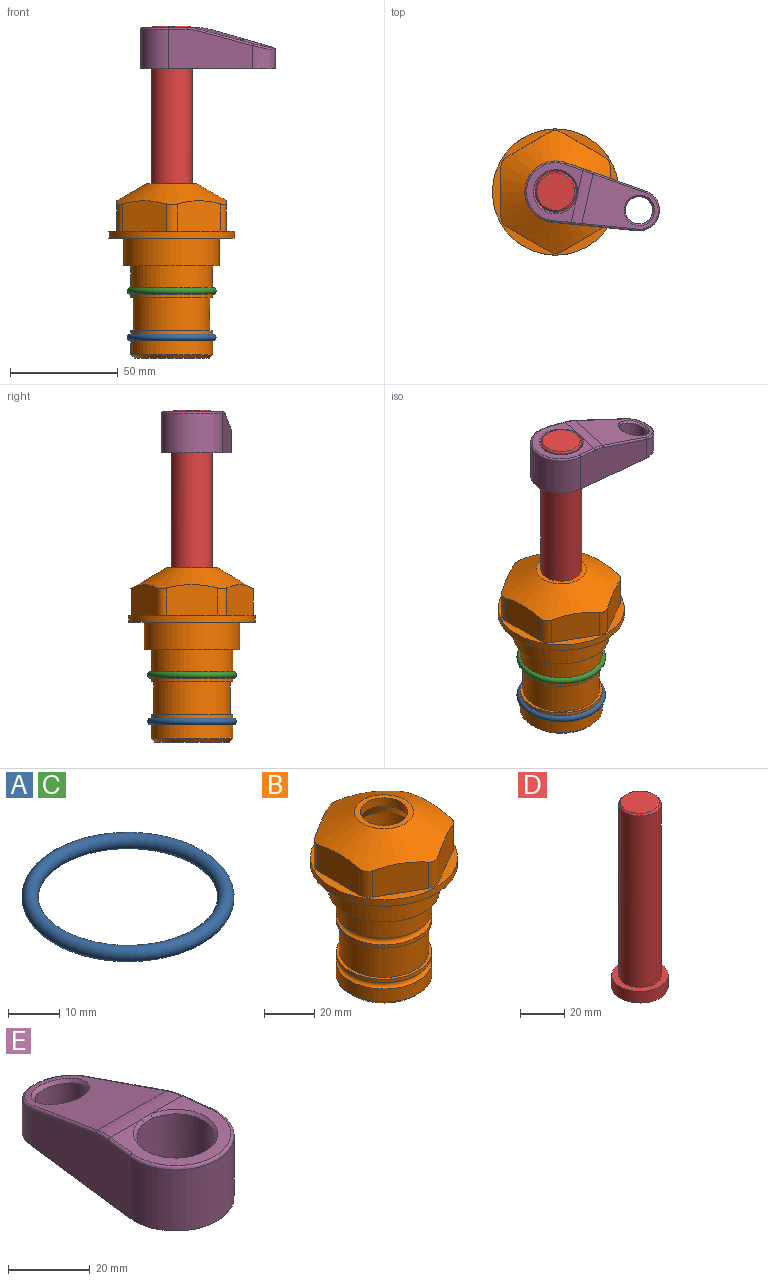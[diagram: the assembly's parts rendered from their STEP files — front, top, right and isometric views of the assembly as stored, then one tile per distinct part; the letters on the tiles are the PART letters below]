
ASSEMBLY  parts=5 mates=4
PART A: 1 faces, bbox 44.7x44.7x3.2 mm
  f0: torus R=19.05mm, axis (0,0,1), area 1193.9mm2
PART B: 36 faces, bbox 58.7x58.7x81 mm
  f0: cylinder r=17.78mm len=35.56mm, axis (0,0,1), area 1670.8mm2, adj f23,f24,f31
  f1: cylinder r=19.05mm len=38.1mm, axis (0,0,1), area 1191.9mm2, adj f26,f27,f30
  f2: plane 58.66x58.66mm, normal (0,0,-1), area 1150.6mm2, adj f3,f28
  f3: cylinder r=29.33mm len=58.66mm, axis (0,0,-1), area 585.1mm2, adj f2,f4
  f4: plane 58.66x58.66mm, normal (0,0,1), area 475.9mm2, adj f3,f5,f6,f7,f8,f9,f10,f11
  f5: plane 20.32x14.34mm, normal (-0.5,0.87,0), area 324.4mm2, adj f4,f15,f16,f17
  f6: plane 20.32x14.34mm, normal (0.5,0.87,0), area 324.4mm2, adj f4,f14,f15,f17
  f7: plane 23.48x14.34mm, normal (1,0,0), area 324.4mm2, adj f4,f13,f14,f17
  f8: plane 20.32x14.34mm, normal (0.5,-0.87,0), area 324.4mm2, adj f4,f12,f13,f17
  f9: plane 20.32x14.34mm, normal (-0.5,-0.87,0), area 324.4mm2, adj f4,f11,f12,f17
  f10: plane 23.48x14.34mm, normal (-1,0,0), area 324.4mm2, adj f4,f11,f16,f17
  f11: cylinder r=5.08mm len=12.85mm, axis (0,0,-1), area 67.2mm2, adj f4,f9,f10,f17
  f12: cylinder r=5.08mm len=12.85mm, axis (0,0,-1), area 67.2mm2, adj f4,f8,f9,f17
  f13: cylinder r=5.08mm len=12.85mm, axis (0,0,-1), area 67.2mm2, adj f4,f7,f8,f17
  f14: cylinder r=5.08mm len=12.85mm, axis (0,0,-1), area 67.2mm2, adj f4,f6,f7,f17
  f15: cylinder r=5.08mm len=12.85mm, axis (0,0,-1), area 67.2mm2, adj f4,f5,f6,f17
  f16: cylinder r=5.08mm len=12.85mm, axis (0,0,-1), area 67.2mm2, adj f4,f5,f10,f17
  f17: cone r=11.73mm half-angle=60deg, axis (0,0,-1), area 2071.8mm2, adj f5,f6,f7,f8,f9,f10,f11,f12
  f18: plane 23.46x23.46mm, normal (0,0,1), area 147.4mm2, adj f17,f35
  f19: plane 34.93x34.93mm, normal (0,0,-1), area 958mm2, adj f29
  f20: cylinder r=19.05mm len=38.1mm, axis (0,0,1), area 760.1mm2, adj f21,f29
  f21: torus R=19.05mm, axis (0,0,1), area 565.3mm2, adj f20,f22
  f22: cylinder r=19.05mm len=38.1mm, axis (0,0,1), area 190mm2, adj f21,f23
  f23: plane 38.1x38.1mm, normal (0,0,1), area 146.9mm2, adj f0,f22
  f24: plane 38.1x38.1mm, normal (0,0,-1), area 146.9mm2, adj f0,f25
  f25: cylinder r=19.05mm len=38.1mm, axis (0,0,1), area 190mm2, adj f24,f26
  f26: torus R=19.05mm, axis (0,0,1), area 565.3mm2, adj f1,f25
  f27: plane 44.45x44.45mm, normal (0,0,-1), area 411.7mm2, adj f1,f28
  f28: cylinder r=22.23mm len=44.45mm, axis (0,0,1), area 1773.5mm2, adj f2,f27
  f29: cone r=19.05mm half-angle=45deg, axis (0,0,1), area 257.5mm2, adj f19,f20
  f30: cylinder r=3.17mm len=6.75mm, axis (-1,0,0), area 128mm2, adj f1,f33
  f31: cylinder r=3.17mm len=6.35mm, axis (-1,0,0), area 102.5mm2, adj f0,f33
  f32: plane 25.4x25.4mm, normal (0,0,1), area 506.7mm2, adj f33
  f33: cylinder r=12.7mm len=66.42mm, axis (0,0,-1), area 5236.2mm2, adj f30,f31,f32,f34
  f34: cone r=9.53mm half-angle=30deg, axis (0,0,-1), area 443.4mm2, adj f33,f35
  f35: cylinder r=9.53mm len=19.05mm, axis (0,0,-1), area 240.9mm2, adj f18,f34
PART C: same geometry as A
PART D: 6 faces, bbox 25.4x25.4x101.6 mm
  f0: plane 17.46x17.46mm, normal (0,0,1), area 239.5mm2, adj f5
  f1: plane 25.4x25.4mm, normal (0,0,-1), area 506.7mm2, adj f2
  f2: cylinder r=12.7mm len=25.4mm, axis (0,0,1), area 506.7mm2, adj f1,f3
  f3: plane 25.4x25.4mm, normal (0,0,1), area 221.7mm2, adj f2,f4
  f4: cylinder r=9.53mm len=94.46mm, axis (0,0,1), area 5653mm2, adj f3,f5
  f5: cone r=8.73mm half-angle=45deg, axis (0,0,-1), area 64.4mm2, adj f0,f4
PART E: 31 faces, bbox 31.7x65.5x19.8 mm
  f0: plane 39.12x18.26mm, normal (0.99,0.12,0), area 612.2mm2, adj f1,f4,f7,f11,f13,f15
  f1: cylinder r=9.53mm len=18.91mm, axis (0,0,-1), area 296.1mm2, adj f0,f2,f7,f17
  f2: plane 39.12x18.26mm, normal (-0.99,0.12,0), area 612.2mm2, adj f1,f4,f7,f12,f14,f16
  f3: cylinder r=6.35mm len=12.7mm, axis (0,0,-1), area 362.4mm2, adj f7,f18
  f4: cylinder r=14.29mm len=28.58mm, axis (0,0,-1), area 882.2mm2, adj f0,f2,f7,f10
  f5: cylinder r=9.53mm len=19.05mm, axis (0,0,-1), area 1092.6mm2, adj f7,f19,f20
  f6: plane 26.99x23.69mm, normal (0,0,1), area 216.2mm2, adj f9,f10,f11,f12,f19
  f7: plane 63.5x28.58mm, normal (0,0,-1), area 661.8mm2, adj f0,f1,f2,f3,f4,f5,f22,f23
  f8: plane 33.52x23.6mm, normal (0,0.26,0.97), area 486mm2, adj f9,f15,f16,f17,f18
  f9: cylinder r=19.05mm len=24.72mm, axis (1,0,0), area 120.4mm2, adj f6,f8,f13,f14,f20
  f10: torus R=13.49mm, axis (0,0,1), area 59mm2, adj f4,f6,f11,f12
  f11: cylinder r=0.79mm len=8.67mm, axis (0.12,-0.99,0), area 10.8mm2, adj f0,f6,f10,f13
  f12: cylinder r=0.79mm len=8.67mm, axis (0.12,0.99,0), area 10.8mm2, adj f2,f6,f10,f14
  f13: bspline ~4.95x1.42mm, area 6.1mm2, adj f0,f9,f11,f15
  f14: bspline ~4.95x1.42mm, area 6.1mm2, adj f2,f9,f12,f16
  f15: cylinder r=0.79mm len=25.95mm, axis (0.12,-0.96,0.26), area 32.9mm2, adj f0,f8,f13,f17
  f16: cylinder r=0.79mm len=25.95mm, axis (0.12,0.96,-0.26), area 32.9mm2, adj f2,f8,f14,f17
  f17: bspline ~18.91x8.38mm, area 30mm2, adj f1,f8,f15,f16
  f18: bspline ~14.29x14.29mm, area 48.3mm2, adj f3,f8
  f19: cone r=9.53mm half-angle=45deg, axis (0,0,1), area 66.5mm2, adj f5,f6,f20
  f20: bspline ~3.22x0.96mm, area 3.5mm2, adj f5,f9,f19
  f21: plane 2.75x2.72mm, normal (0,0,-1), area 2.9mm2, adj f23,f25,f28
  f22: plane 23.05x15.88mm, normal (-0.99,-0.12,0), area 323.6mm2, adj f7,f25,f26,f27,f28,f29
  f23: plane 23.05x15.88mm, normal (0.99,-0.12,0), area 323.6mm2, adj f7,f21,f25,f27,f28,f30
  f24: cylinder r=9.53mm len=10.69mm, axis (0,0,-1), area 114.7mm2, adj f7,f27,f29,f30
  f25: cylinder r=12.7mm len=20.59mm, axis (0,0,-1), area 381.1mm2, adj f7,f21,f22,f23,f26,f28
  f26: plane 2.75x2.72mm, normal (0,0,-1), area 2.9mm2, adj f22,f25,f28
  f27: plane 19.72x18.37mm, normal (0,-0.26,-0.97), area 291.8mm2, adj f22,f23,f24,f28,f29,f30
  f28: cylinder r=15.88mm len=19.92mm, axis (1,0,0), area 54.8mm2, adj f21,f22,f23,f25,f26,f27
  f29: cylinder r=1.59mm len=11mm, axis (0,0,-1), area 34.7mm2, adj f7,f22,f24,f27
  f30: cylinder r=1.59mm len=11mm, axis (0,0,-1), area 34.7mm2, adj f7,f23,f24,f27
PLACE A t=(0,0,-21.59)mm
PLACE B at identity fixed
PLACE C at identity
PLACE D rot(axis=(0,0,-1),102.6deg) t=(0,0,35.17)mm
PLACE E rot(axis=(0,0,-1),102.6deg) t=(0,0,34.38)mm
MATE fastened D.f2 <-> E.f4  axis (0,0,1) through (0,0,97.88)mm
MATE cylindrical B.f0 <-> D.f2  axis (0,0,1) through (0,0,-42.93)mm
MATE fastened C.f0 <-> B.f0  axis (0,0,1) through (0,0,-24.51)mm
MATE fastened A.f0 <-> B.f0  axis (0,0,1) through (0,0,-46.1)mm
